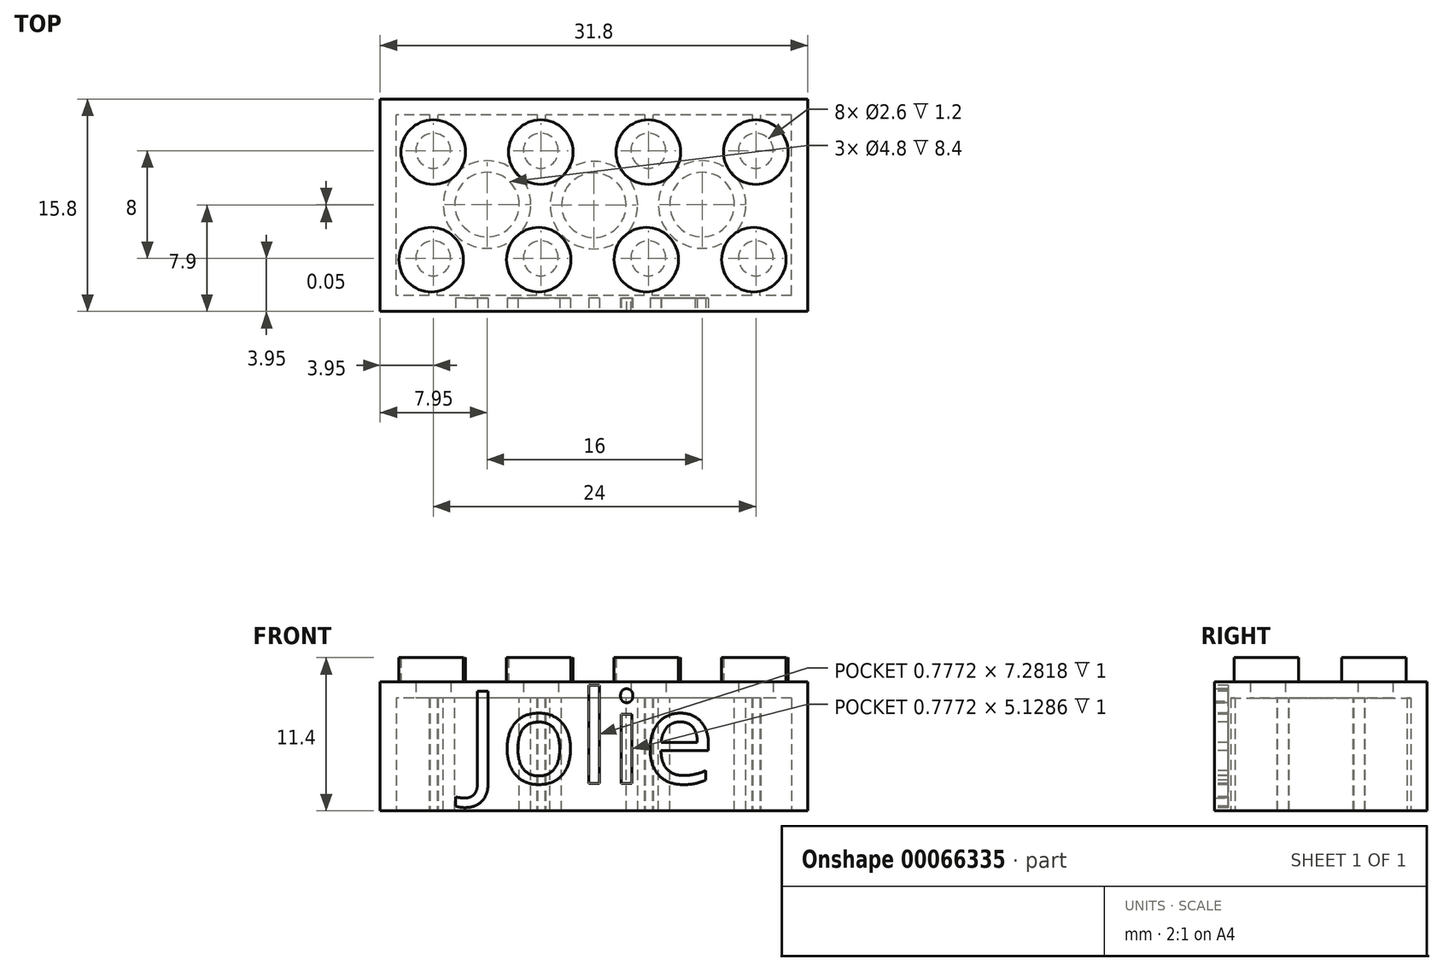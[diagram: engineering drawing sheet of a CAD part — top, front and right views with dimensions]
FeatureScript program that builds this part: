
annotation { "Feature Type Name" : "Feature", "Feature Type Description" : "" }
export const myFeature = defineFeature(function(context is Context, id is Id, definition is map)
    precondition{}
    {
        {
            var Q0;
            Q0=qCreatedBy(makeId("Top.planeOp"),FACE);
            var sketch = newSketch(context, id + "F0", { "sketchPlane" : qUnion([Q0])});
            skLineSegment(sketch, "E0.rect.bottom", {"start": v(15.9, -7.9) * mm, "end": v(-15.9, -7.9) * mm});
            skLineSegment(sketch, "E0.rect.top", {"start": v(15.9, 7.9) * mm, "end": v(-15.9, 7.9) * mm});
            skLineSegment(sketch, "E0.rect.left", {"start": v(15.9, -7.9) * mm, "end": v(15.9, 7.9) * mm});
            skLineSegment(sketch, "E0.rect.right", {"start": v(-15.9, -7.9) * mm, "end": v(-15.9, 7.9) * mm});
            skPoint(sketch, "E0.rect.middle", {"position": v(0, 0) * mm});
            skSolve(sketch);
        }
        {
            var Q0;
            Q0 = qSketchRegion(id + "F0", true);
            extrude(context, id + "F1", {"entities" : qUnion([Q0]), "depth" : 9.6 * mm});
        }
        {
            var Q0;
            Q0=qCreatedBy(makeId("Top.planeOp"),FACE);
            var sketch = newSketch(context, id + "F2", { "sketchPlane" : qUnion([Q0])});
            skLineSegment(sketch, "E1.rect.bottom", {"start": v(14.7, -6.7) * mm, "end": v(-14.7, -6.7) * mm});
            skLineSegment(sketch, "E1.rect.top", {"start": v(14.7, 6.7) * mm, "end": v(-14.7, 6.7) * mm});
            skLineSegment(sketch, "E1.rect.left", {"start": v(14.7, -6.7) * mm, "end": v(14.7, 6.7) * mm});
            skLineSegment(sketch, "E1.rect.right", {"start": v(-14.7, -6.7) * mm, "end": v(-14.7, 6.7) * mm});
            skPoint(sketch, "E1.rect.middle", {"position": v(0, 0) * mm});
            skSolve(sketch);
        }
        {
            var Q0;
            Q0 = qSketchRegion(id + "F2", true);
            extrude(context, id + "F3", {"entities" : qUnion([Q0]), "operationType" : NewBodyOperationType.REMOVE, "depth" : 8.4 * mm});
        }
        {
            var Q0;
            Q0=makeQuery(id+"F1.opExtrude","CAP_FACE",FACE,{"disambiguationData":[OSD([sQuery(id+"F0.wireOp",EDGE,"E0.rect.bottom"),sQuery(id+"F0.wireOp",EDGE,"E0.rect.top"),sQuery(id+"F0.wireOp",EDGE,"E0.rect.left"),sQuery(id+"F0.wireOp",EDGE,"E0.rect.right")])],"isStart":false});
            var sketch = newSketch(context, id + "F4", { "sketchPlane" : qUnion([Q0])});
            skLineSegment(sketch, "E2", {"start": v(-22.67, 0) * mm, "end": v(0, 0) * mm, "construction": true});
            skLineSegment(sketch, "E3", {"start": v(0, 0) * mm, "end": v(20.1, -0.03) * mm, "construction": true});
            skCircle(sketch, "E4", {"center": v(-11.95, 3.95) * mm, "radius": 2.4 * mm});
            skCircle(sketch, "E5.0.1.0", {"center": v(-12.1, -4.05) * mm, "radius": 2.4 * mm});
            skCircle(sketch, "E5.1.0.0", {"center": v(-3.95, 3.95) * mm, "radius": 2.4 * mm});
            skCircle(sketch, "E5.1.1.0", {"center": v(-4.1, -4.05) * mm, "radius": 2.4 * mm});
            skCircle(sketch, "E5.2.0.0", {"center": v(4.05, 3.95) * mm, "radius": 2.4 * mm});
            skCircle(sketch, "E5.2.1.0", {"center": v(3.9, -4.05) * mm, "radius": 2.4 * mm});
            skCircle(sketch, "E5.3.0.0", {"center": v(12.05, 3.95) * mm, "radius": 2.4 * mm});
            skCircle(sketch, "E5.3.1.0", {"center": v(11.9, -4.05) * mm, "radius": 2.4 * mm});
            skLineSegment(sketch, "E5.direction1", {"start": v(-11.95, 3.95) * mm, "end": v(-3.95, 3.95) * mm, "construction": true});
            skLineSegment(sketch, "E5.direction2", {"start": v(-11.95, 3.95) * mm, "end": v(-12.1, -4.05) * mm, "construction": true});
            skSolve(sketch);
        }
        {
            var Q0;
            Q0=makeQuery(id+"F4.imprint","IMPRINT",FACE,{"disambiguationData":[TD([[makeQuery(id+"F4.imprint","IMPRINT",EDGE,{"derivedFrom":sQuery(id+"F4.wireOp",EDGE,"E4")}),1.0]])]});
            var Q1;
            Q1=makeQuery(id+"F4.imprint","IMPRINT",FACE,{"disambiguationData":[TD([[makeQuery(id+"F4.imprint","IMPRINT",EDGE,{"derivedFrom":sQuery(id+"F4.wireOp",EDGE,"E5.0.1.0")}),1.0]])]});
            var Q2;
            Q2=makeQuery(id+"F4.imprint","IMPRINT",FACE,{"disambiguationData":[TD([[makeQuery(id+"F4.imprint","IMPRINT",EDGE,{"derivedFrom":sQuery(id+"F4.wireOp",EDGE,"E5.1.0.0")}),1.0]])]});
            var Q3;
            Q3=makeQuery(id+"F4.imprint","IMPRINT",FACE,{"disambiguationData":[TD([[makeQuery(id+"F4.imprint","IMPRINT",EDGE,{"derivedFrom":sQuery(id+"F4.wireOp",EDGE,"E5.1.1.0")}),1.0]])]});
            var Q4;
            Q4=makeQuery(id+"F4.imprint","IMPRINT",FACE,{"disambiguationData":[TD([[makeQuery(id+"F4.imprint","IMPRINT",EDGE,{"derivedFrom":sQuery(id+"F4.wireOp",EDGE,"E5.2.0.0")}),1.0]])]});
            var Q5;
            Q5=makeQuery(id+"F4.imprint","IMPRINT",FACE,{"disambiguationData":[TD([[makeQuery(id+"F4.imprint","IMPRINT",EDGE,{"derivedFrom":sQuery(id+"F4.wireOp",EDGE,"E5.2.1.0")}),1.0]])]});
            var Q6;
            Q6=makeQuery(id+"F4.imprint","IMPRINT",FACE,{"disambiguationData":[TD([[makeQuery(id+"F4.imprint","IMPRINT",EDGE,{"derivedFrom":sQuery(id+"F4.wireOp",EDGE,"E5.3.0.0")}),1.0]])]});
            var Q7;
            Q7=makeQuery(id+"F4.imprint","IMPRINT",FACE,{"disambiguationData":[TD([[makeQuery(id+"F4.imprint","IMPRINT",EDGE,{"derivedFrom":sQuery(id+"F4.wireOp",EDGE,"E5.3.1.0")}),1.0]])]});
            extrude(context, id + "F5", {"entities" : qUnion([Q0, Q1, Q2, Q3, Q4, Q5, Q6, Q7]), "operationType" : NewBodyOperationType.ADD, "depth" : 1.8 * mm});
        }
        {
            var Q0;
            Q0=qCreatedBy(makeId("Top.planeOp"),FACE);
            var Q1;
            Q1 = qBodyType(qCreatedBy(id + "F9" ,EDGE), BodyType.WIRE);
            cPlane(context, id + "F6", {"entities" : qUnion([Q0, Q1]), "cplaneType" : CPlaneType.OFFSET, "offset" : 8.4 * mm, "width" : 150 * mm, "height" : 150 * mm});
        }
        {
            var Q0;
            Q0=qCreatedBy(id+"F6.planeOp",FACE);
            var sketch = newSketch(context, id + "F7", { "sketchPlane" : qUnion([Q0])});
            skCircle(sketch, "E6", {"center": v(-11.95, -3.95) * mm, "radius": 1.3 * mm});
            skCircle(sketch, "E7.0.1.0", {"center": v(-11.95, 4.05) * mm, "radius": 1.3 * mm});
            skCircle(sketch, "E7.1.0.0", {"center": v(-3.95, -3.95) * mm, "radius": 1.3 * mm});
            skCircle(sketch, "E7.1.1.0", {"center": v(-3.95, 4.05) * mm, "radius": 1.3 * mm});
            skCircle(sketch, "E7.2.0.0", {"center": v(4.05, -3.95) * mm, "radius": 1.3 * mm});
            skCircle(sketch, "E7.2.1.0", {"center": v(4.05, 4.05) * mm, "radius": 1.3 * mm});
            skCircle(sketch, "E7.3.0.0", {"center": v(12.05, -3.95) * mm, "radius": 1.3 * mm});
            skCircle(sketch, "E7.3.1.0", {"center": v(12.05, 4.05) * mm, "radius": 1.3 * mm});
            skLineSegment(sketch, "E7.direction1", {"start": v(-11.95, -3.95) * mm, "end": v(-3.95, -3.95) * mm, "construction": true});
            skLineSegment(sketch, "E7.direction2", {"start": v(-11.95, -3.95) * mm, "end": v(-11.95, 4.05) * mm, "construction": true});
            skSolve(sketch);
        }
        {
            var Q0;
            Q0 = qSketchRegion(id + "F7", true);
            extrude(context, id + "F8", {"entities" : qUnion([Q0]), "operationType" : NewBodyOperationType.REMOVE, "depth" : 1.2 * mm});
        }
        {
            var Q0;
            Q0=qCreatedBy(id+"F6.planeOp",FACE);
            var sketch = newSketch(context, id + "F9", { "sketchPlane" : qUnion([Q0])});
            skLineSegment(sketch, "E8", {"start": v(-11.95, -3.95) * mm, "end": v(-3.82, 4.01) * mm, "construction": true});
            skLineSegment(sketch, "E9", {"start": v(-3.95, -3.95) * mm, "end": v(-11.95, 4.05) * mm, "construction": true});
            skLineSegment(sketch, "E10", {"start": v(4.05, -3.95) * mm, "end": v(12.05, 4.05) * mm, "construction": true});
            skLineSegment(sketch, "E11", {"start": v(12.05, -3.95) * mm, "end": v(4.05, 4.05) * mm, "construction": true});
            skCircle(sketch, "E12", {"center": v(-7.95, 0.05) * mm, "radius": 3.25 * mm});
            skCircle(sketch, "E13", {"center": v(8.05, 0.05) * mm, "radius": 3.25 * mm});
            skCircle(sketch, "E14", {"center": v(-7.95, 0.05) * mm, "radius": 2.4 * mm});
            skCircle(sketch, "E15", {"center": v(8.05, 0.05) * mm, "radius": 2.4 * mm});
            skLineSegment(sketch, "E16", {"start": v(-3.95, -3.95) * mm, "end": v(4.05, 4.05) * mm, "construction": true});
            skLineSegment(sketch, "E17", {"start": v(-3.82, 4.01) * mm, "end": v(4.05, -3.95) * mm, "construction": true});
            skCircle(sketch, "E18", {"center": v(0, 0) * mm, "radius": 3.25 * mm});
            skCircle(sketch, "E19", {"center": v(0, 0) * mm, "radius": 2.4 * mm});
            skSolve(sketch);
        }
        {
            var Q0;
            Q0 = qSketchRegion(id + "F9", true);
            var Q1;
            Q1=makeQuery(id+"F1.opExtrude","CAP_FACE",FACE,{"disambiguationData":[OSD([sQuery(id+"F0.wireOp",EDGE,"E0.rect.bottom"),sQuery(id+"F0.wireOp",EDGE,"E0.rect.top"),sQuery(id+"F0.wireOp",EDGE,"E0.rect.left"),sQuery(id+"F0.wireOp",EDGE,"E0.rect.right")])],"isStart":true});
            extrude(context, id + "F10", {"entities" : qUnion([Q0]), "endBound" : BoundingType.UP_TO_SURFACE, "oppositeDirection" : true, "endBoundEntityFace" : qUnion([Q1]), "depth" : mm});
        }
        {
            var Q0;
            Q0=makeQuery(id+"F0.imprint","IMPRINT",FACE,{"disambiguationData":[TD([[makeQuery(id+"F0.imprint","IMPRINT",EDGE,{"derivedFrom":sQuery(id+"F0.wireOp",EDGE,"E0.rect.bottom")}),-1.0]])]});
            var sketch = newSketch(context, id + "F11", { "sketchPlane" : qUnion([Q0])});
            skLineSegment(sketch, "E20.bottom", {"start": v(-12.25, -6.7) * mm, "end": v(-11.65, -6.7) * mm});
            skLineSegment(sketch, "E20.top", {"start": v(-12.25, -6.4) * mm, "end": v(-11.65, -6.4) * mm});
            skLineSegment(sketch, "E20.left", {"start": v(-12.25, -6.7) * mm, "end": v(-12.25, -6.4) * mm});
            skLineSegment(sketch, "E20.right", {"start": v(-11.65, -6.7) * mm, "end": v(-11.65, -6.4) * mm});
            skLineSegment(sketch, "E21", {"start": v(-11.95, -13.4) * mm, "end": v(-11.95, 4.05) * mm, "construction": true});
            skLineSegment(sketch, "E22.1.0.0", {"start": v(-4.25, -6.7) * mm, "end": v(-4.25, -6.4) * mm});
            skLineSegment(sketch, "E22.1.0.1", {"start": v(-4.25, -6.7) * mm, "end": v(-3.65, -6.7) * mm});
            skLineSegment(sketch, "E22.1.0.2", {"start": v(-3.65, -6.7) * mm, "end": v(-3.65, -6.4) * mm});
            skLineSegment(sketch, "E22.1.0.3", {"start": v(-4.25, -6.4) * mm, "end": v(-3.65, -6.4) * mm});
            skLineSegment(sketch, "E22.2.0.0", {"start": v(3.75, -6.7) * mm, "end": v(3.75, -6.4) * mm});
            skLineSegment(sketch, "E22.2.0.1", {"start": v(3.75, -6.7) * mm, "end": v(4.35, -6.7) * mm});
            skLineSegment(sketch, "E22.2.0.2", {"start": v(4.35, -6.7) * mm, "end": v(4.35, -6.4) * mm});
            skLineSegment(sketch, "E22.2.0.3", {"start": v(3.75, -6.4) * mm, "end": v(4.35, -6.4) * mm});
            skLineSegment(sketch, "E22.direction1", {"start": v(-12.25, -6.7) * mm, "end": v(-4.25, -6.7) * mm, "construction": true});
            skLineSegment(sketch, "E23.0.3.0", {"start": v(11.75, -6.7) * mm, "end": v(11.75, -6.4) * mm});
            skLineSegment(sketch, "E23.3.3.0", {"start": v(11.75, -6.7) * mm, "end": v(12.35, -6.7) * mm});
            skLineSegment(sketch, "E23.6.3.0", {"start": v(12.35, -6.7) * mm, "end": v(12.35, -6.4) * mm});
            skLineSegment(sketch, "E23.9.3.0", {"start": v(11.75, -6.4) * mm, "end": v(12.35, -6.4) * mm});
            skLineSegment(sketch, "E24", {"start": v(-11.95, -3.95) * mm, "end": v(-11.87, 10.58) * mm, "construction": true});
            skLineSegment(sketch, "E25.bottom", {"start": v(-12.2, 6.4) * mm, "end": v(-11.6, 6.4) * mm});
            skLineSegment(sketch, "E25.top", {"start": v(-12.2, 6.7) * mm, "end": v(-11.6, 6.7) * mm});
            skLineSegment(sketch, "E25.left", {"start": v(-12.2, 6.4) * mm, "end": v(-12.2, 6.7) * mm});
            skLineSegment(sketch, "E25.right", {"start": v(-11.6, 6.4) * mm, "end": v(-11.6, 6.7) * mm});
            skLineSegment(sketch, "E26.1.0.0", {"start": v(-4.2, 6.4) * mm, "end": v(-3.6, 6.4) * mm});
            skLineSegment(sketch, "E26.1.0.1", {"start": v(-4.2, 6.4) * mm, "end": v(-4.2, 6.7) * mm});
            skLineSegment(sketch, "E26.1.0.2", {"start": v(-4.2, 6.7) * mm, "end": v(-3.6, 6.7) * mm});
            skLineSegment(sketch, "E26.1.0.3", {"start": v(-3.6, 6.4) * mm, "end": v(-3.6, 6.7) * mm});
            skLineSegment(sketch, "E26.2.0.0", {"start": v(3.8, 6.4) * mm, "end": v(4.4, 6.4) * mm});
            skLineSegment(sketch, "E26.2.0.1", {"start": v(3.8, 6.4) * mm, "end": v(3.8, 6.7) * mm});
            skLineSegment(sketch, "E26.2.0.2", {"start": v(3.8, 6.7) * mm, "end": v(4.4, 6.7) * mm});
            skLineSegment(sketch, "E26.2.0.3", {"start": v(4.4, 6.4) * mm, "end": v(4.4, 6.7) * mm});
            skLineSegment(sketch, "E26.3.0.0", {"start": v(11.8, 6.4) * mm, "end": v(12.4, 6.4) * mm});
            skLineSegment(sketch, "E26.3.0.1", {"start": v(11.8, 6.4) * mm, "end": v(11.8, 6.7) * mm});
            skLineSegment(sketch, "E26.3.0.2", {"start": v(11.8, 6.7) * mm, "end": v(12.4, 6.7) * mm});
            skLineSegment(sketch, "E26.3.0.3", {"start": v(12.4, 6.4) * mm, "end": v(12.4, 6.7) * mm});
            skLineSegment(sketch, "E26.direction1", {"start": v(-12.2, 6.4) * mm, "end": v(-4.2, 6.4) * mm, "construction": true});
            skSolve(sketch);
        }
        {
            var Q0;
            Q0 = qSketchRegion(id + "F11", true);
            extrude(context, id + "F12", {"entities" : qUnion([Q0]), "operationType" : NewBodyOperationType.ADD, "depth" : 9.6 * mm});
        }
        {
            var Q0;
            Q0=qCreatedBy(id+"F6.planeOp",FACE);
            var sketch = newSketch(context, id + "F13", { "sketchPlane" : qUnion([Q0])});
            skLineSegment(sketch, "E27.bottom", {"start": v(-0.3, -6.7) * mm, "end": v(0.3, -6.7) * mm});
            skLineSegment(sketch, "E27.top", {"start": v(-0.3, -2.7) * mm, "end": v(0.3, -2.7) * mm});
            skLineSegment(sketch, "E27.left", {"start": v(-0.3, -6.7) * mm, "end": v(-0.3, -2.7) * mm});
            skLineSegment(sketch, "E27.right", {"start": v(0.3, -6.7) * mm, "end": v(0.3, -2.7) * mm});
            skLineSegment(sketch, "E28.bottom", {"start": v(-0.3, 2.75) * mm, "end": v(0.3, 2.75) * mm});
            skLineSegment(sketch, "E28.top", {"start": v(-0.3, 6.75) * mm, "end": v(0.3, 6.75) * mm});
            skLineSegment(sketch, "E28.left", {"start": v(-0.3, 2.75) * mm, "end": v(-0.3, 6.75) * mm});
            skLineSegment(sketch, "E28.right", {"start": v(0.3, 2.75) * mm, "end": v(0.3, 6.75) * mm});
            skSolve(sketch);
        }
        {
            var Q0;
            Q0=sQuery(id+"F13.wireOp",EDGE,"E27.bottom");
            var Q1;
            Q1=sQuery(id+"F13.wireOp",EDGE,"E27.left");
            var Q2;
            Q2=sQuery(id+"F13.wireOp",EDGE,"E27.right");
            var Q3;
            Q3=sQuery(id+"F13.wireOp",EDGE,"E27.top");
            var Q4;
            Q4=sQuery(id+"F13.wireOp",EDGE,"E28.right");
            var Q5;
            Q5=sQuery(id+"F13.wireOp",EDGE,"E28.top");
            var Q6;
            Q6=sQuery(id+"F13.wireOp",EDGE,"E28.bottom");
            var Q7;
            Q7=sQuery(id+"F13.wireOp",EDGE,"E28.left");
            extrude(context, id + "F14", {"bodyType" : ToolBodyType.SURFACE, "surfaceEntities" : qUnion([Q0, Q1, Q2, Q3, Q4, Q5, Q6, Q7]), "oppositeDirection" : true, "depth" : 6.4 * mm});
        }
        {
            var Q0;
            Q0=makeQuery(id+"F1.opExtrude","SWEPT_FACE",FACE,{"disambiguationData":[OSD([sQuery(id+"F0.wireOp",EDGE,"E0.rect.bottom")])]});
            var sketch = newSketch(context, id + "F15", { "sketchPlane" : qUnion([Q0])});
            skText(sketch, "E29", { "text": "Jolie", "fontName": "OpenSans-Regular.ttf"});
            const initialGuessF15  = {"E29": [-0.00955, 0.00205, 1, 0, 0.0069]};
            skSetInitialGuess(sketch, initialGuessF15);
            skSolve(sketch);
        }
        {
            var Q0;
            Q0 = qSketchRegion(id + "F15", true);
            extrude(context, id + "F16", {"entities" : qUnion([Q0]), "operationType" : NewBodyOperationType.REMOVE, "oppositeDirection" : true, "depth" : 1 * mm});
        }
    });
